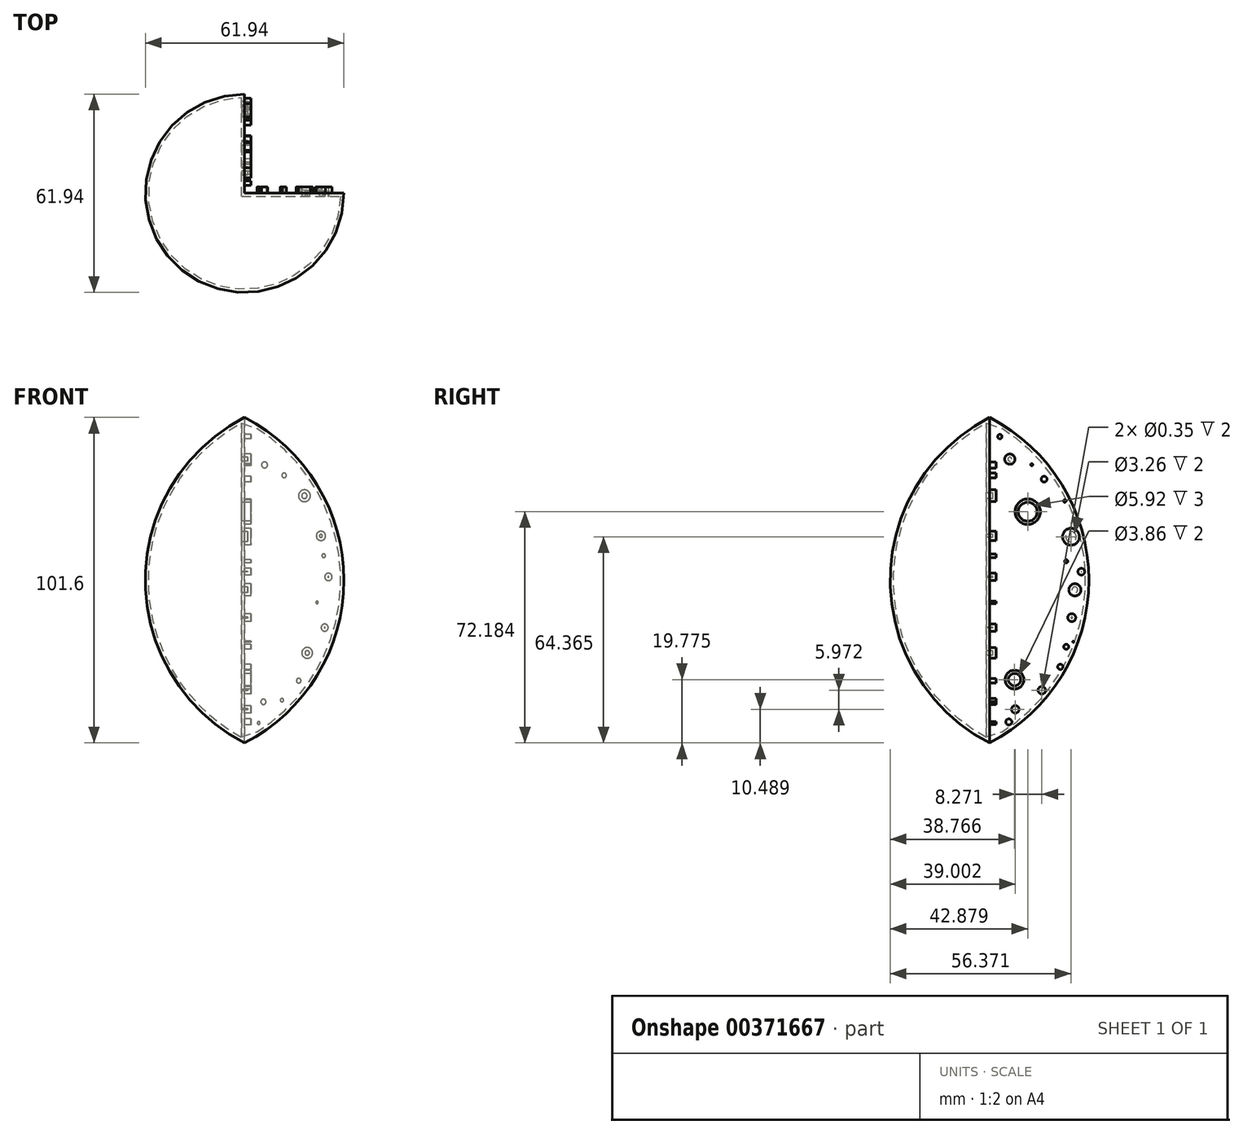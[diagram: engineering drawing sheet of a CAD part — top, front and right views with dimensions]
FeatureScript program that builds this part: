
annotation { "Feature Type Name" : "Feature", "Feature Type Description" : "" }
export const myFeature = defineFeature(function(context is Context, id is Id, definition is map)
    precondition{}
    {
        {
            var Q0;
            Q0=qCreatedBy(makeId("Front.planeOp"),FACE);
            var sketch = newSketch(context, id + "F0", { "sketchPlane" : qUnion([Q0])});
            skLineSegment(sketch, "E0", {"start": v(0, 50.8) * mm, "end": v(0, 0) * mm});
            skLineSegment(sketch, "E1", {"start": v(0, 0) * mm, "end": v(0, -50.8) * mm});
            skArc(sketch, "E2", {"start": v(0, -50.8) * mm, "mid": v(30.97, 0) * mm, "end": v(0, 50.8) * mm});
            skSolve(sketch);
        }
        {
            var Q0;
            Q0 = qSketchRegion(id + "F0", true);
            var Q1;
            Q1=sQuery(id+"F0.wireOp",EDGE,"E1");
            revolve(context, id + "F1", {"entities" : qUnion([Q0]), "axis" : qUnion([Q1]), "revolveType" : RevolveType.ONE_DIRECTION, "angle" : 270 * degree});
        }
        {
            var Q0;
            Q0=makeQuery(id+"F1.opRevolve","CAP_FACE",FACE,{"disambiguationData":[OSD([sQuery(id+"F0.wireOp",EDGE,"E0"),sQuery(id+"F0.wireOp",EDGE,"E1"),sQuery(id+"F0.wireOp",EDGE,"E2")])],"isStart":true});
            var sketch = newSketch(context, id + "F2", { "sketchPlane" : qUnion([Q0])});
            skCircle(sketch, "E3", {"center": v(-23.82, 13.83) * mm, "radius": 1.45 * mm});
            skSolve(sketch);
        }
        {
            var Q0;
            Q0 = qSketchRegion(id + "F2", true);
            extrude(context, id + "F3", {"entities" : qUnion([Q0]), "operationType" : NewBodyOperationType.ADD, "depth" : 2 * mm});
        }
        {
            var Q0;
            Q0=makeQuery(id+"F1.opRevolve","CAP_FACE",FACE,{"disambiguationData":[OSD([sQuery(id+"F0.wireOp",EDGE,"E0"),sQuery(id+"F0.wireOp",EDGE,"E1"),sQuery(id+"F0.wireOp",EDGE,"E2")])],"isStart":true});
            var sketch = newSketch(context, id + "F4", { "sketchPlane" : qUnion([Q0])});
            skCircle(sketch, "E4", {"center": v(-6.23, 35.97) * mm, "radius": 0.94 * mm});
            skSolve(sketch);
        }
        {
            var Q0;
            Q0 = qSketchRegion(id + "F4", true);
            extrude(context, id + "F5", {"entities" : qUnion([Q0]), "operationType" : NewBodyOperationType.ADD, "depth" : 2 * mm});
        }
        {
            var Q0;
            Q0=makeQuery(id+"F1.opRevolve","CAP_FACE",FACE,{"disambiguationData":[OSD([sQuery(id+"F0.wireOp",EDGE,"E0"),sQuery(id+"F0.wireOp",EDGE,"E1"),sQuery(id+"F0.wireOp",EDGE,"E2")])],"isStart":true});
            var sketch = newSketch(context, id + "F6", { "sketchPlane" : qUnion([Q0])});
            skCircle(sketch, "E5", {"center": v(-18.66, 26.36) * mm, "radius": 1.85 * mm});
            skSolve(sketch);
        }
        {
            var Q0;
            Q0 = qSketchRegion(id + "F6", true);
            extrude(context, id + "F7", {"entities" : qUnion([Q0]), "operationType" : NewBodyOperationType.ADD, "depth" : 2 * mm});
        }
        {
            var Q0;
            Q0=makeQuery(id+"F1.opRevolve","CAP_FACE",FACE,{"disambiguationData":[OSD([sQuery(id+"F0.wireOp",EDGE,"E0"),sQuery(id+"F0.wireOp",EDGE,"E1"),sQuery(id+"F0.wireOp",EDGE,"E2")])],"isStart":true});
            var sketch = newSketch(context, id + "F8", { "sketchPlane" : qUnion([Q0])});
            skCircle(sketch, "E6", {"center": v(-26.14, 1.02) * mm, "radius": 1.15 * mm});
            skSolve(sketch);
        }
        {
            var Q0;
            Q0 = qSketchRegion(id + "F8", true);
            extrude(context, id + "F9", {"entities" : qUnion([Q0]), "operationType" : NewBodyOperationType.ADD, "depth" : 2 * mm});
        }
        {
            var Q0;
            Q0=makeQuery(id+"F1.opRevolve","CAP_FACE",FACE,{"disambiguationData":[OSD([sQuery(id+"F0.wireOp",EDGE,"E0"),sQuery(id+"F0.wireOp",EDGE,"E1"),sQuery(id+"F0.wireOp",EDGE,"E2")])],"isStart":true});
            var sketch = newSketch(context, id + "F10", { "sketchPlane" : qUnion([Q0])});
            skCircle(sketch, "E7", {"center": v(-19.53, -22.69) * mm, "radius": 1.7 * mm});
            skSolve(sketch);
        }
        {
            var Q0;
            Q0 = qSketchRegion(id + "F10", true);
            extrude(context, id + "F11", {"entities" : qUnion([Q0]), "operationType" : NewBodyOperationType.ADD, "depth" : 2 * mm});
        }
        {
            var Q0;
            Q0=makeQuery(id+"F1.opRevolve","CAP_FACE",FACE,{"disambiguationData":[OSD([sQuery(id+"F0.wireOp",EDGE,"E0"),sQuery(id+"F0.wireOp",EDGE,"E1"),sQuery(id+"F0.wireOp",EDGE,"E2")])],"isStart":true});
            var sketch = newSketch(context, id + "F12", { "sketchPlane" : qUnion([Q0])});
            skCircle(sketch, "E8", {"center": v(-5.86, -37.96) * mm, "radius": 0.82 * mm});
            skSolve(sketch);
        }
        {
            var Q0;
            Q0 = qSketchRegion(id + "F12", true);
            extrude(context, id + "F13", {"entities" : qUnion([Q0]), "operationType" : NewBodyOperationType.ADD, "depth" : 2 * mm});
        }
        {
            var Q0;
            Q0=makeQuery(id+"F1.opRevolve","CAP_FACE",FACE,{"disambiguationData":[OSD([sQuery(id+"F0.wireOp",EDGE,"E0"),sQuery(id+"F0.wireOp",EDGE,"E1"),sQuery(id+"F0.wireOp",EDGE,"E2")])],"isStart":true});
            var sketch = newSketch(context, id + "F14", { "sketchPlane" : qUnion([Q0])});
            skCircle(sketch, "E9", {"center": v(-16.87, -31.37) * mm, "radius": 0.73 * mm});
            skSolve(sketch);
        }
        {
            var Q0;
            Q0 = qSketchRegion(id + "F14", true);
            extrude(context, id + "F15", {"entities" : qUnion([Q0]), "operationType" : NewBodyOperationType.ADD, "depth" : 2 * mm});
        }
        {
            var Q0;
            Q0=makeQuery(id+"F1.opRevolve","CAP_FACE",FACE,{"disambiguationData":[OSD([sQuery(id+"F0.wireOp",EDGE,"E0"),sQuery(id+"F0.wireOp",EDGE,"E1"),sQuery(id+"F0.wireOp",EDGE,"E2")])],"isStart":true});
            var sketch = newSketch(context, id + "F16", { "sketchPlane" : qUnion([Q0])});
            skCircle(sketch, "E10", {"center": v(-12.33, 32.7) * mm, "radius": 0.71 * mm});
            skSolve(sketch);
        }
        {
            var Q0;
            Q0 = qSketchRegion(id + "F16", true);
            extrude(context, id + "F17", {"entities" : qUnion([Q0]), "operationType" : NewBodyOperationType.ADD, "depth" : 2 * mm});
        }
        {
            var Q0;
            Q0=makeQuery(id+"F1.opRevolve","CAP_FACE",FACE,{"disambiguationData":[OSD([sQuery(id+"F0.wireOp",EDGE,"E0"),sQuery(id+"F0.wireOp",EDGE,"E1"),sQuery(id+"F0.wireOp",EDGE,"E2")])],"isStart":true});
            var sketch = newSketch(context, id + "F18", { "sketchPlane" : qUnion([Q0])});
            skCircle(sketch, "E11", {"center": v(-24.68, 7.66) * mm, "radius": 0.57 * mm});
            skSolve(sketch);
        }
        {
            var Q0;
            Q0 = qSketchRegion(id + "F18", true);
            extrude(context, id + "F19", {"entities" : qUnion([Q0]), "operationType" : NewBodyOperationType.ADD, "depth" : 2 * mm});
        }
        {
            var Q0;
            Q0=makeQuery(id+"F1.opRevolve","CAP_FACE",FACE,{"disambiguationData":[OSD([sQuery(id+"F0.wireOp",EDGE,"E0"),sQuery(id+"F0.wireOp",EDGE,"E1"),sQuery(id+"F0.wireOp",EDGE,"E2")])],"isStart":true});
            var sketch = newSketch(context, id + "F20", { "sketchPlane" : qUnion([Q0])});
            skCircle(sketch, "E12", {"center": v(-22.59, -6.94) * mm, "radius": 0.38 * mm});
            skSolve(sketch);
        }
        {
            var Q0;
            Q0 = qSketchRegion(id + "F20", true);
            extrude(context, id + "F21", {"entities" : qUnion([Q0]), "operationType" : NewBodyOperationType.ADD, "depth" : 2 * mm});
        }
        {
            var Q0;
            Q0=makeQuery(id+"F1.opRevolve","CAP_FACE",FACE,{"disambiguationData":[OSD([sQuery(id+"F0.wireOp",EDGE,"E0"),sQuery(id+"F0.wireOp",EDGE,"E1"),sQuery(id+"F0.wireOp",EDGE,"E2")])],"isStart":true});
            var sketch = newSketch(context, id + "F22", { "sketchPlane" : qUnion([Q0])});
            skCircle(sketch, "E13", {"center": v(-24.99, -14.79) * mm, "radius": 1.1 * mm});
            skSolve(sketch);
        }
        {
            var Q0;
            Q0 = qSketchRegion(id + "F22", true);
            extrude(context, id + "F23", {"entities" : qUnion([Q0]), "operationType" : NewBodyOperationType.ADD, "depth" : 2 * mm});
        }
        {
            var Q0;
            Q0=makeQuery(id+"F1.opRevolve","CAP_FACE",FACE,{"disambiguationData":[OSD([sQuery(id+"F0.wireOp",EDGE,"E0"),sQuery(id+"F0.wireOp",EDGE,"E1"),sQuery(id+"F0.wireOp",EDGE,"E2")])],"isStart":true});
            var sketch = newSketch(context, id + "F24", { "sketchPlane" : qUnion([Q0])});
            skCircle(sketch, "E14", {"center": v(-11.67, -37.44) * mm, "radius": 0.52 * mm});
            skSolve(sketch);
        }
        {
            var Q0;
            Q0 = qSketchRegion(id + "F24", true);
            extrude(context, id + "F25", {"entities" : qUnion([Q0]), "operationType" : NewBodyOperationType.ADD, "depth" : 2 * mm});
        }
        {
            var Q0;
            Q0=makeQuery(id+"F1.opRevolve","CAP_FACE",FACE,{"disambiguationData":[OSD([sQuery(id+"F0.wireOp",EDGE,"E0"),sQuery(id+"F0.wireOp",EDGE,"E1"),sQuery(id+"F0.wireOp",EDGE,"E2")])],"isStart":true});
            var sketch = newSketch(context, id + "F26", { "sketchPlane" : qUnion([Q0])});
            skCircle(sketch, "E15", {"center": v(-4.38, -44.58) * mm, "radius": 0.43 * mm});
            skSolve(sketch);
        }
        {
            var Q0;
            Q0 = qSketchRegion(id + "F26", true);
            extrude(context, id + "F27", {"entities" : qUnion([Q0]), "operationType" : NewBodyOperationType.ADD, "depth" : 2 * mm});
        }
        {
            var Q0;
            Q0=makeQuery(id+"F1.opRevolve","CAP_FACE",FACE,{"disambiguationData":[OSD([sQuery(id+"F0.wireOp",EDGE,"E0"),sQuery(id+"F0.wireOp",EDGE,"E1"),sQuery(id+"F0.wireOp",EDGE,"E2")])],"isStart":false});
            var sketch = newSketch(context, id + "F28", { "sketchPlane" : qUnion([Q0])});
            skCircle(sketch, "E16", {"center": v(6.31, 37.78) * mm, "radius": 1.6 * mm});
            skSolve(sketch);
        }
        {
            var Q0;
            Q0 = qSketchRegion(id + "F28", true);
            extrude(context, id + "F29", {"entities" : qUnion([Q0]), "operationType" : NewBodyOperationType.ADD, "depth" : 2 * mm});
        }
        {
            var Q0;
            Q0=makeQuery(id+"F1.opRevolve","CAP_FACE",FACE,{"disambiguationData":[OSD([sQuery(id+"F0.wireOp",EDGE,"E0"),sQuery(id+"F0.wireOp",EDGE,"E1"),sQuery(id+"F0.wireOp",EDGE,"E2")])],"isStart":false});
            var sketch = newSketch(context, id + "F30", { "sketchPlane" : qUnion([Q0])});
            skCircle(sketch, "E17", {"center": v(13.15, 36.07) * mm, "radius": 0.31 * mm});
            skSolve(sketch);
        }
        {
            var Q0;
            Q0 = qSketchRegion(id + "F30", true);
            extrude(context, id + "F31", {"entities" : qUnion([Q0]), "operationType" : NewBodyOperationType.ADD, "depth" : 2 * mm});
        }
        {
            var Q0;
            Q0=makeQuery(id+"F1.opRevolve","CAP_FACE",FACE,{"disambiguationData":[OSD([sQuery(id+"F0.wireOp",EDGE,"E0"),sQuery(id+"F0.wireOp",EDGE,"E1"),sQuery(id+"F0.wireOp",EDGE,"E2")])],"isStart":false});
            var sketch = newSketch(context, id + "F32", { "sketchPlane" : qUnion([Q0])});
            skCircle(sketch, "E18", {"center": v(17.02, 31.54) * mm, "radius": 0.9 * mm});
            skSolve(sketch);
        }
        {
            var Q0;
            Q0 = qSketchRegion(id + "F32", true);
            extrude(context, id + "F33", {"entities" : qUnion([Q0]), "operationType" : NewBodyOperationType.ADD, "depth" : 2 * mm});
        }
        {
            var Q0;
            Q0=makeQuery(id+"F1.opRevolve","CAP_FACE",FACE,{"disambiguationData":[OSD([sQuery(id+"F0.wireOp",EDGE,"E0"),sQuery(id+"F0.wireOp",EDGE,"E1"),sQuery(id+"F0.wireOp",EDGE,"E2")])],"isStart":false});
            var sketch = newSketch(context, id + "F34", { "sketchPlane" : qUnion([Q0])});
            skCircle(sketch, "E19", {"center": v(23.47, 24.72) * mm, "radius": 0.4 * mm});
            skSolve(sketch);
        }
        {
            var Q0;
            Q0 = qSketchRegion(id + "F34", true);
            extrude(context, id + "F35", {"entities" : qUnion([Q0]), "operationType" : NewBodyOperationType.ADD, "depth" : 2 * mm});
        }
        {
            var Q0;
            Q0=makeQuery(id+"F1.opRevolve","CAP_FACE",FACE,{"disambiguationData":[OSD([sQuery(id+"F0.wireOp",EDGE,"E0"),sQuery(id+"F0.wireOp",EDGE,"E1"),sQuery(id+"F0.wireOp",EDGE,"E2")])],"isStart":false});
            var sketch = newSketch(context, id + "F36", { "sketchPlane" : qUnion([Q0])});
            skCircle(sketch, "E20", {"center": v(25.4, 13.56) * mm, "radius": 2.63 * mm});
            skSolve(sketch);
        }
        {
            var Q0;
            Q0 = qSketchRegion(id + "F36", true);
            extrude(context, id + "F37", {"entities" : qUnion([Q0]), "operationType" : NewBodyOperationType.ADD, "depth" : 2 * mm});
        }
        {
            var Q0;
            Q0=makeQuery(id+"F1.opRevolve","CAP_FACE",FACE,{"disambiguationData":[OSD([sQuery(id+"F0.wireOp",EDGE,"E0"),sQuery(id+"F0.wireOp",EDGE,"E1"),sQuery(id+"F0.wireOp",EDGE,"E2")])],"isStart":false});
            var sketch = newSketch(context, id + "F38", { "sketchPlane" : qUnion([Q0])});
            skCircle(sketch, "E21", {"center": v(28.63, 2.66) * mm, "radius": 1.05 * mm});
            skSolve(sketch);
        }
        {
            var Q0;
            Q0 = qSketchRegion(id + "F38", true);
            extrude(context, id + "F39", {"entities" : qUnion([Q0]), "operationType" : NewBodyOperationType.ADD, "depth" : 2 * mm});
        }
        {
            var Q0;
            Q0=makeQuery(id+"F1.opRevolve","CAP_FACE",FACE,{"disambiguationData":[OSD([sQuery(id+"F0.wireOp",EDGE,"E0"),sQuery(id+"F0.wireOp",EDGE,"E1"),sQuery(id+"F0.wireOp",EDGE,"E2")])],"isStart":false});
            var sketch = newSketch(context, id + "F40", { "sketchPlane" : qUnion([Q0])});
            skCircle(sketch, "E22", {"center": v(23.92, 5.91) * mm, "radius": 0.5 * mm});
            skSolve(sketch);
        }
        {
            var Q0;
            Q0 = qSketchRegion(id + "F40", true);
            extrude(context, id + "F41", {"entities" : qUnion([Q0]), "operationType" : NewBodyOperationType.ADD, "depth" : 2 * mm});
        }
        {
            var Q0;
            Q0=makeQuery(id+"F1.opRevolve","CAP_FACE",FACE,{"disambiguationData":[OSD([sQuery(id+"F0.wireOp",EDGE,"E0"),sQuery(id+"F0.wireOp",EDGE,"E1"),sQuery(id+"F0.wireOp",EDGE,"E2")])],"isStart":false});
            var sketch = newSketch(context, id + "F42", { "sketchPlane" : qUnion([Q0])});
            skCircle(sketch, "E23", {"center": v(26.62, -3) * mm, "radius": 1.9 * mm});
            skSolve(sketch);
        }
        {
            var Q0;
            Q0 = qSketchRegion(id + "F42", true);
            extrude(context, id + "F43", {"entities" : qUnion([Q0]), "operationType" : NewBodyOperationType.ADD, "depth" : 2 * mm});
        }
        {
            var Q0;
            Q0=makeQuery(id+"F1.opRevolve","CAP_FACE",FACE,{"disambiguationData":[OSD([sQuery(id+"F0.wireOp",EDGE,"E0"),sQuery(id+"F0.wireOp",EDGE,"E1"),sQuery(id+"F0.wireOp",EDGE,"E2")])],"isStart":false});
            var sketch = newSketch(context, id + "F44", { "sketchPlane" : qUnion([Q0])});
            skCircle(sketch, "E24", {"center": v(25.64, -11.68) * mm, "radius": 1.24 * mm});
            skSolve(sketch);
        }
        {
            var Q0;
            Q0 = qSketchRegion(id + "F44", true);
            extrude(context, id + "F45", {"entities" : qUnion([Q0]), "operationType" : NewBodyOperationType.ADD, "depth" : 2 * mm});
        }
        {
            var Q0;
            Q0=makeQuery(id+"F1.opRevolve","CAP_FACE",FACE,{"disambiguationData":[OSD([sQuery(id+"F0.wireOp",EDGE,"E0"),sQuery(id+"F0.wireOp",EDGE,"E1"),sQuery(id+"F0.wireOp",EDGE,"E2")])],"isStart":false});
            var sketch = newSketch(context, id + "F46", { "sketchPlane" : qUnion([Q0])});
            skCircle(sketch, "E25", {"center": v(22.07, -27.03) * mm, "radius": 0.81 * mm});
            skSolve(sketch);
        }
        {
            var Q0;
            Q0 = qSketchRegion(id + "F46", true);
            extrude(context, id + "F47", {"entities" : qUnion([Q0]), "operationType" : NewBodyOperationType.ADD, "depth" : 2 * mm});
        }
        {
            var Q0;
            Q0=makeQuery(id+"F1.opRevolve","CAP_FACE",FACE,{"disambiguationData":[OSD([sQuery(id+"F0.wireOp",EDGE,"E0"),sQuery(id+"F0.wireOp",EDGE,"E1"),sQuery(id+"F0.wireOp",EDGE,"E2")])],"isStart":false});
            var sketch = newSketch(context, id + "F48", { "sketchPlane" : qUnion([Q0])});
            skCircle(sketch, "E26", {"center": v(26.12, -19.2) * mm, "radius": 0.19 * mm});
            skSolve(sketch);
        }
        {
            var Q0;
            Q0 = qSketchRegion(id + "F48", true);
            extrude(context, id + "F49", {"entities" : qUnion([Q0]), "operationType" : NewBodyOperationType.ADD, "depth" : 2 * mm});
        }
        {
            var Q0;
            Q0=makeQuery(id+"F1.opRevolve","CAP_FACE",FACE,{"disambiguationData":[OSD([sQuery(id+"F0.wireOp",EDGE,"E0"),sQuery(id+"F0.wireOp",EDGE,"E1"),sQuery(id+"F0.wireOp",EDGE,"E2")])],"isStart":false});
            var sketch = newSketch(context, id + "F50", { "sketchPlane" : qUnion([Q0])});
            skCircle(sketch, "E27", {"center": v(23.92, -20.77) * mm, "radius": 0.77 * mm});
            skSolve(sketch);
        }
        {
            var Q0;
            Q0 = qSketchRegion(id + "F50", true);
            extrude(context, id + "F51", {"entities" : qUnion([Q0]), "operationType" : NewBodyOperationType.ADD, "depth" : 2 * mm});
        }
        {
            var Q0;
            Q0=makeQuery(id+"F1.opRevolve","CAP_FACE",FACE,{"disambiguationData":[OSD([sQuery(id+"F0.wireOp",EDGE,"E0"),sQuery(id+"F0.wireOp",EDGE,"E1"),sQuery(id+"F0.wireOp",EDGE,"E2")])],"isStart":false});
            var sketch = newSketch(context, id + "F52", { "sketchPlane" : qUnion([Q0])});
            skCircle(sketch, "E28", {"center": v(16.3, -34.34) * mm, "radius": 1.18 * mm});
            skSolve(sketch);
        }
        {
            var Q0;
            Q0 = qSketchRegion(id + "F52", true);
            extrude(context, id + "F53", {"entities" : qUnion([Q0]), "operationType" : NewBodyOperationType.ADD, "depth" : 2 * mm});
        }
        {
            var Q0;
            Q0=makeQuery(id+"F1.opRevolve","CAP_FACE",FACE,{"disambiguationData":[OSD([sQuery(id+"F0.wireOp",EDGE,"E0"),sQuery(id+"F0.wireOp",EDGE,"E1"),sQuery(id+"F0.wireOp",EDGE,"E2")])],"isStart":false});
            var sketch = newSketch(context, id + "F54", { "sketchPlane" : qUnion([Q0])});
            skCircle(sketch, "E29", {"center": v(8.03, -40.31) * mm, "radius": 1.18 * mm});
            skSolve(sketch);
        }
        {
            var Q0;
            Q0 = qSketchRegion(id + "F54", true);
            extrude(context, id + "F55", {"entities" : qUnion([Q0]), "operationType" : NewBodyOperationType.ADD, "depth" : 2 * mm});
        }
        {
            var Q0;
            Q0=makeQuery(id+"F1.opRevolve","CAP_FACE",FACE,{"disambiguationData":[OSD([sQuery(id+"F0.wireOp",EDGE,"E0"),sQuery(id+"F0.wireOp",EDGE,"E1"),sQuery(id+"F0.wireOp",EDGE,"E2")])],"isStart":false});
            var sketch = newSketch(context, id + "F56", { "sketchPlane" : qUnion([Q0])});
            skCircle(sketch, "E30", {"center": v(6.01, -44.23) * mm, "radius": 0.95 * mm});
            skSolve(sketch);
        }
        {
            var Q0;
            Q0 = qSketchRegion(id + "F56", true);
            extrude(context, id + "F57", {"entities" : qUnion([Q0]), "operationType" : NewBodyOperationType.ADD, "depth" : 2 * mm});
        }
        {
            var Q0;
            Q0=makeQuery(id+"F1.opRevolve","CAP_FACE",FACE,{"disambiguationData":[OSD([sQuery(id+"F0.wireOp",EDGE,"E0"),sQuery(id+"F0.wireOp",EDGE,"E1"),sQuery(id+"F0.wireOp",EDGE,"E2")])],"isStart":false});
            var sketch = newSketch(context, id + "F58", { "sketchPlane" : qUnion([Q0])});
            skCircle(sketch, "E31", {"center": v(3.21, 44.83) * mm, "radius": 0.68 * mm});
            skSolve(sketch);
        }
        {
            var Q0;
            Q0 = qSketchRegion(id + "F58", true);
            extrude(context, id + "F59", {"entities" : qUnion([Q0]), "operationType" : NewBodyOperationType.ADD, "depth" : 2 * mm});
        }
        {
            var Q0;
            Q0=makeQuery(id+"F1.opRevolve","CAP_FACE",FACE,{"disambiguationData":[OSD([sQuery(id+"F0.wireOp",EDGE,"E0"),sQuery(id+"F0.wireOp",EDGE,"E1"),sQuery(id+"F0.wireOp",EDGE,"E2")])],"isStart":false});
            var sketch = newSketch(context, id + "F60", { "sketchPlane" : qUnion([Q0])});
            skCircle(sketch, "E32", {"center": v(11.9, 21.38) * mm, "radius": 3.96 * mm});
            skSolve(sketch);
        }
        {
            var Q0;
            Q0 = qSketchRegion(id + "F60", true);
            extrude(context, id + "F61", {"entities" : qUnion([Q0]), "operationType" : NewBodyOperationType.ADD, "depth" : 2 * mm});
        }
        {
            var Q0;
            Q0=makeQuery(id+"F61.opExtrude","CAP_FACE",FACE,{"disambiguationData":[OSD([sQuery(id+"F60.wireOp",EDGE,"E32")])],"isStart":false});
            shell(context, id + "F62", {"entities" : qUnion([Q0]), "thickness" : 1 * mm});
        }
        {
            var Q0;
            Q0=makeQuery(id+"F1.opRevolve","CAP_FACE",FACE,{"disambiguationData":[OSD([sQuery(id+"F0.wireOp",EDGE,"E0"),sQuery(id+"F0.wireOp",EDGE,"E1"),sQuery(id+"F0.wireOp",EDGE,"E2")])],"isStart":true});
            var sketch = newSketch(context, id + "F63", { "sketchPlane" : qUnion([Q0])});
            skFitSpline(sketch, "E33", {"points": [v(0, 11.54) * mm, v(-3.57, 13.28) * mm, v(-7.18, 17.16) * mm, v(-12.67, 21.92) * mm, v(-15.6, 18.8) * mm, v(-18.1, 11.26) * mm, v(-18.96, 3.62) * mm, v(-17.34, -2.97) * mm, v(-14.68, -8.68) * mm, v(-15.74, -13.24) * mm, v(-15.22, -16.7) * mm, v(-11.8, -22.99) * mm, v(-8.01, -25.87) * mm, v(-2.99, -25.53) * mm, v(0, -27.05) * mm], "startDerivative": vector(-61.76, 23.88) * mm, "endDerivative": vector(47.63, -37.52) * mm});
            skSolve(sketch);
        }
        {
            var Q0;
            Q0 = qSketchRegion(id + "F63", true);
            var Q1;
            Q1=sQuery(id+"F63.wireOp",EDGE,"E33");
            extrude(context, id + "F64", {"entities" : qUnion([Q0]), "bodyType" : ToolBodyType.SURFACE, "surfaceEntities" : qUnion([Q1]), "depth" : 2 * mm});
        }
        {
            var Q0;
            Q0=makeQuery(id+"F1.opRevolve","CAP_FACE",FACE,{"disambiguationData":[OSD([sQuery(id+"F0.wireOp",EDGE,"E0"),sQuery(id+"F0.wireOp",EDGE,"E1"),sQuery(id+"F0.wireOp",EDGE,"E2")])],"isStart":false});
            var sketch = newSketch(context, id + "F65", { "sketchPlane" : qUnion([Q0])});
            skFitSpline(sketch, "E34", {"points": [v(0, 12.03) * mm, v(5.97, 10.9) * mm, v(13.73, 8.93) * mm, v(14.77, 3.97) * mm, v(8.84, 0) * mm, v(18.92, -4.18) * mm, v(17.76, -12.55) * mm, v(11.74, -18.62) * mm, v(6.65, -23.17) * mm, v(0, -27.21) * mm], "startDerivative": vector(55.64, -12.98) * mm, "endDerivative": vector(-62.29, -33.94) * mm});
            skSolve(sketch);
        }
        {
            var Q0;
            Q0 = qSketchRegion(id + "F65", true);
            var Q1;
            Q1=sQuery(id+"F65.wireOp",EDGE,"E34");
            extrude(context, id + "F66", {"entities" : qUnion([Q0]), "bodyType" : ToolBodyType.SURFACE, "surfaceEntities" : qUnion([Q1]), "depth" : 2 * mm});
        }
        {
            var Q0;
            Q0=makeQuery(id+"F1.opRevolve","CAP_FACE",FACE,{"disambiguationData":[OSD([sQuery(id+"F0.wireOp",EDGE,"E0"),sQuery(id+"F0.wireOp",EDGE,"E1"),sQuery(id+"F0.wireOp",EDGE,"E2")])],"isStart":false});
            var sketch = newSketch(context, id + "F67", { "sketchPlane" : qUnion([Q0])});
            skSolve(sketch);
        }
        {
            var Q0;
            Q0=makeQuery(id+"F67.imprint","IMPRINT",FACE,{"disambiguationData":[TD([[makeQuery(id+"F67.imprint","IMPRINT",EDGE,{"derivedFrom":makeQuery(id+"F1.opRevolve","CAP_EDGE",EDGE,{"disambiguationData":[OSD([sQuery(id+"F0.wireOp",EDGE,"E2")])],"isStart":false})}),1.0]])]});
            var sketch = newSketch(context, id + "F68", { "sketchPlane" : qUnion([Q0])});
            skFitSpline(sketch, "E35", {"points": [v(0, 6.55) * mm, v(5.82, 6.84) * mm, v(9.61, 4.8) * mm, v(4.91, 1.27) * mm, v(4.93, -5.38) * mm, v(10.18, -7.32) * mm, v(12.09, -10.02) * mm, v(5.44, -13.35) * mm, v(3.42, -19) * mm, v(0, -20.52) * mm], "startDerivative": vector(47.58, 9.05) * mm, "endDerivative": vector(-44.75, -7.23) * mm});
            skSolve(sketch);
        }
        {
            var Q0;
            Q0 = qSketchRegion(id + "F68", true);
            var Q1;
            Q1=sQuery(id+"F68.wireOp",EDGE,"E35");
            extrude(context, id + "F69", {"entities" : qUnion([Q0]), "bodyType" : ToolBodyType.SURFACE, "surfaceEntities" : qUnion([Q1]), "depth" : 2 * mm});
        }
        {
            var Q0;
            Q0=makeQuery(id+"F1.opRevolve","CAP_FACE",FACE,{"disambiguationData":[OSD([sQuery(id+"F0.wireOp",EDGE,"E0"),sQuery(id+"F0.wireOp",EDGE,"E1"),sQuery(id+"F0.wireOp",EDGE,"E2")])],"isStart":true});
            var sketch = newSketch(context, id + "F70", { "sketchPlane" : qUnion([Q0])});
            skFitSpline(sketch, "E36", {"points": [v(0, 6.79) * mm, v(-5.05, 6.83) * mm, v(-9.25, 10.88) * mm, v(-11.85, 6.12) * mm, v(-11.16, 0) * mm, v(-4.85, -3.54) * mm, v(-6.2, -9.94) * mm, v(-8.78, -14.46) * mm, v(-9.06, -18.97) * mm, v(-3.06, -22.14) * mm, v(0, -20.46) * mm], "startDerivative": vector(-55.44, -15.62) * mm, "endDerivative": vector(31.57, 31.11) * mm});
            skSolve(sketch);
        }
        {
            var Q0;
            {var subQ0=sQuery(id+"F70.wireOp",EDGE,"E36");Q0=makeQuery(id+"F70.imprint","IMPRINT",FACE,{"disambiguationData":[TD([[makeQuery(id+"F70.imprint","IMPRINT",EDGE,{"derivedFrom":subQ0}),-1.0]])]});}
            var Q1;
            Q1=sQuery(id+"F70.wireOp",EDGE,"E36");
            extrude(context, id + "F71", {"entities" : qUnion([Q0]), "bodyType" : ToolBodyType.SURFACE, "surfaceEntities" : qUnion([Q1]), "depth" : 2 * mm});
        }
        {
            var Q0;
            Q0=makeQuery(id+"F67.imprint","IMPRINT",FACE,{"disambiguationData":[TD([[makeQuery(id+"F67.imprint","IMPRINT",EDGE,{"derivedFrom":makeQuery(id+"F1.opRevolve","CAP_EDGE",EDGE,{"disambiguationData":[OSD([sQuery(id+"F0.wireOp",EDGE,"E2")])],"isStart":false})}),1.0]])]});
            var sketch = newSketch(context, id + "F72", { "sketchPlane" : qUnion([Q0])});
            skCircle(sketch, "E37", {"center": v(7.8, -31.03) * mm, "radius": 2.93 * mm});
            skSolve(sketch);
        }
        {
            var Q0;
            Q0 = qSketchRegion(id + "F72", true);
            extrude(context, id + "F73", {"entities" : qUnion([Q0]), "operationType" : NewBodyOperationType.ADD, "depth" : 2 * mm});
        }
        {
            var Q0;
            Q0=makeQuery(id+"F73.opExtrude","CAP_FACE",FACE,{"disambiguationData":[OSD([sQuery(id+"F72.wireOp",EDGE,"E37")])],"isStart":false});
            shell(context, id + "F74", {"entities" : qUnion([Q0]), "thickness" : 1 * mm});
        }
        {
            var Q0;
            Q0=qCreatedBy(makeId("Right.planeOp"),FACE);
            var sketch = newSketch(context, id + "F75", { "sketchPlane" : qUnion([Q0])});
            skFitSpline(sketch, "E38", {"points": [v(-2.44, 48.7) * mm, v(-11.68, 60.41) * mm, v(-5.2, 68.59) * mm, v(-12.52, 78.38) * mm, v(-11.22, 91.52) * mm, v(-18.77, 100) * mm, v(-13.74, 107.12) * mm], "startDerivative": vector(-82.95, 65.28) * mm, "endDerivative": vector(60.22, 50.69) * mm});
            skSolve(sketch);
        }
        {
            var Q0;
            Q0 = qSketchRegion(id + "F75", true);
            var Q1;
            Q1=sQuery(id+"F75.wireOp",EDGE,"E38");
            extrude(context, id + "F76", {"entities" : qUnion([Q0]), "bodyType" : ToolBodyType.SURFACE, "surfaceEntities" : qUnion([Q1]), "depth" : 2 * mm});
        }
        {
            var Q0;
            Q0=qCreatedBy(makeId("Top.planeOp"),FACE);
            var sketch = newSketch(context, id + "F77", { "sketchPlane" : qUnion([Q0])});
            skFitSpline(sketch, "E39", {"points": [v(-3.68, 30.38) * mm, v(-9.63, 51.58) * mm, v(0, 52.21) * mm, v(3.13, 45.07) * mm], "startDerivative": vector(-29.88, 59.94) * mm, "endDerivative": vector(4.31, -32.14) * mm});
            skSolve(sketch);
        }
        {
            var Q0;
            Q0 = qSketchRegion(id + "F77", true);
            var Q1;
            Q1=sQuery(id+"F77.wireOp",EDGE,"E39");
            extrude(context, id + "F78", {"entities" : qUnion([Q0]), "bodyType" : ToolBodyType.SURFACE, "surfaceEntities" : qUnion([Q1]), "depth" : 2 * mm});
        }
    });
